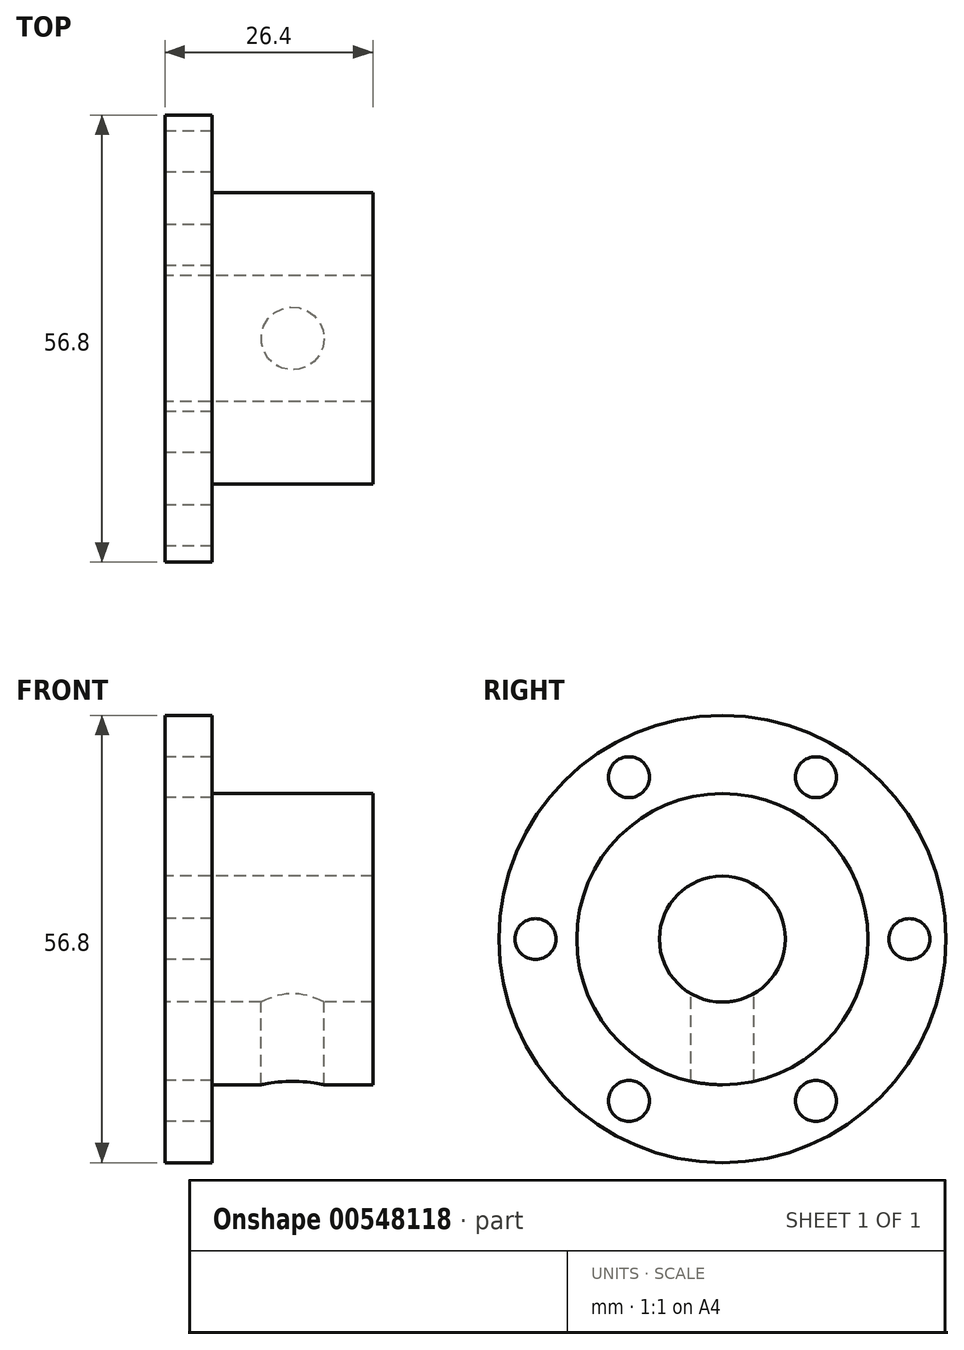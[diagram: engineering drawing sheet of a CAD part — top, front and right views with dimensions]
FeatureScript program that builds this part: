
annotation { "Feature Type Name" : "Feature", "Feature Type Description" : "" }
export const myFeature = defineFeature(function(context is Context, id is Id, definition is map)
    precondition{}
    {
        {
            var Q0;
            Q0=qCreatedBy(makeId("Front.planeOp"),FACE);
            var sketch = newSketch(context, id + "F0", { "sketchPlane" : qUnion([Q0])});
            skLineSegment(sketch, "E0", {"start": v(0, 0) * mm, "end": v(116.92, 0) * mm});
            skLineSegment(sketch, "E1", {"start": v(0, 0) * mm, "end": v(0, 8) * mm});
            skLineSegment(sketch, "E2", {"start": v(0, 8) * mm, "end": v(0, 28.4) * mm});
            skLineSegment(sketch, "E3", {"start": v(0, 28.4) * mm, "end": v(6, 28.4) * mm});
            skLineSegment(sketch, "E4", {"start": v(6, 28.4) * mm, "end": v(6, 18.5) * mm});
            skLineSegment(sketch, "E5", {"start": v(6, 18.5) * mm, "end": v(26.4, 18.5) * mm});
            skLineSegment(sketch, "E6", {"start": v(0, 8) * mm, "end": v(26.4, 8) * mm});
            skLineSegment(sketch, "E7", {"start": v(26.4, 8) * mm, "end": v(26.4, 18.5) * mm});
            skSolve(sketch);
        }
        {
            var Q0;
            Q0 = qSketchRegion(id + "F0", true);
            var Q1;
            Q1=sQuery(id+"F0.wireOp",EDGE,"E0");
            revolve(context, id + "F1", {"entities" : qUnion([Q0]), "axis" : qUnion([Q1]), "revolveType" : RevolveType.FULL});
        }
        {
            var Q0;
            Q0=qCreatedBy(makeId("Right.planeOp"),FACE);
            var sketch = newSketch(context, id + "F2", { "sketchPlane" : qUnion([Q0])});
            skLineSegment(sketch, "E8", {"start": v(0, 0) * mm, "end": v(-28.29, 0) * mm, "construction": true});
            skCircle(sketch, "E9", {"center": v(0, 0) * mm, "radius": 23.75 * mm, "construction": true});
            skCircle(sketch, "E10", {"center": v(-23.75, 0) * mm, "radius": 2.6 * mm});
            skCircle(sketch, "E11.1.0", {"center": v(-11.88, -20.57) * mm, "radius": 2.6 * mm});
            skCircle(sketch, "E11.2.0", {"center": v(11.87, -20.57) * mm, "radius": 2.6 * mm});
            skCircle(sketch, "E11.3.0", {"center": v(23.75, 0) * mm, "radius": 2.6 * mm});
            skCircle(sketch, "E11.4.0", {"center": v(11.88, 20.57) * mm, "radius": 2.6 * mm});
            skCircle(sketch, "E11.5.0", {"center": v(-11.88, 20.57) * mm, "radius": 2.6 * mm});
            skSolve(sketch);
        }
        {
            var Q0;
            Q0=makeQuery(id+"F2.imprint","IMPRINT",FACE,{"disambiguationData":[TD([[makeQuery(id+"F2.imprint","IMPRINT",EDGE,{"derivedFrom":sQuery(id+"F2.wireOp",EDGE,"E11.4.0")}),1.0]])]});
            var Q1;
            Q1=makeQuery(id+"F2.imprint","IMPRINT",FACE,{"disambiguationData":[TD([[makeQuery(id+"F2.imprint","IMPRINT",EDGE,{"derivedFrom":sQuery(id+"F2.wireOp",EDGE,"E11.3.0")}),1.0]])]});
            var Q2;
            Q2=makeQuery(id+"F2.imprint","IMPRINT",FACE,{"disambiguationData":[TD([[makeQuery(id+"F2.imprint","IMPRINT",EDGE,{"derivedFrom":sQuery(id+"F2.wireOp",EDGE,"E11.2.0")}),1.0]])]});
            var Q3;
            Q3=makeQuery(id+"F2.imprint","IMPRINT",FACE,{"disambiguationData":[TD([[makeQuery(id+"F2.imprint","IMPRINT",EDGE,{"derivedFrom":sQuery(id+"F2.wireOp",EDGE,"E11.1.0")}),1.0]])]});
            var Q4;
            Q4=makeQuery(id+"F2.imprint","IMPRINT",FACE,{"disambiguationData":[TD([[makeQuery(id+"F2.imprint","IMPRINT",EDGE,{"derivedFrom":sQuery(id+"F2.wireOp",EDGE,"E10")}),1.0]])]});
            var Q5;
            Q5=makeQuery(id+"F2.imprint","IMPRINT",FACE,{"disambiguationData":[TD([[makeQuery(id+"F2.imprint","IMPRINT",EDGE,{"derivedFrom":sQuery(id+"F2.wireOp",EDGE,"E11.5.0")}),1.0]])]});
            var Q6;
            Q6=sQuery(id+"F2.wireOp",EDGE,"E11.3.0");
            var Q7;
            Q7=sQuery(id+"F2.wireOp",EDGE,"E11.2.0");
            var Q8;
            Q8=sQuery(id+"F2.wireOp",EDGE,"E11.1.0");
            var Q9;
            Q9=sQuery(id+"F2.wireOp",EDGE,"E10");
            var Q10;
            Q10=sQuery(id+"F2.wireOp",EDGE,"E11.4.0");
            var Q11;
            Q11=sQuery(id+"F2.wireOp",EDGE,"E11.5.0");
            extrude(context, id + "F3", {"entities" : qUnion([Q0, Q1, Q2, Q3, Q4, Q5]), "operationType" : NewBodyOperationType.REMOVE, "surfaceEntities" : qUnion([Q6, Q7, Q8, Q9, Q10, Q11]), "endBound" : BoundingType.UP_TO_NEXT, "depth" : 25 * mm, "offsetDistance" : 25 * mm});
        }
        {
            var Q0;
            Q0=qCreatedBy(makeId("Top.planeOp"),FACE);
            var sketch = newSketch(context, id + "F4", { "sketchPlane" : qUnion([Q0])});
            skLineSegment(sketch, "E12", {"start": v(0, 0) * mm, "end": v(16.2, 0) * mm, "construction": true});
            skCircle(sketch, "E13", {"center": v(16.2, 0) * mm, "radius": 4 * mm});
            skSolve(sketch);
        }
        {
            var Q0;
            Q0=makeQuery(id+"F4.imprint","IMPRINT",FACE,{"disambiguationData":[TD([[makeQuery(id+"F4.imprint","IMPRINT",EDGE,{"derivedFrom":sQuery(id+"F4.wireOp",EDGE,"E13")}),1.0]])]});
            var Q1;
            Q1=sQuery(id+"F4.wireOp",EDGE,"E13");
            extrude(context, id + "F5", {"entities" : qUnion([Q0]), "operationType" : NewBodyOperationType.REMOVE, "surfaceEntities" : qUnion([Q1]), "endBound" : BoundingType.THROUGH_ALL, "oppositeDirection" : true, "depth" : 25 * mm, "offsetDistance" : 25 * mm});
        }
    });
